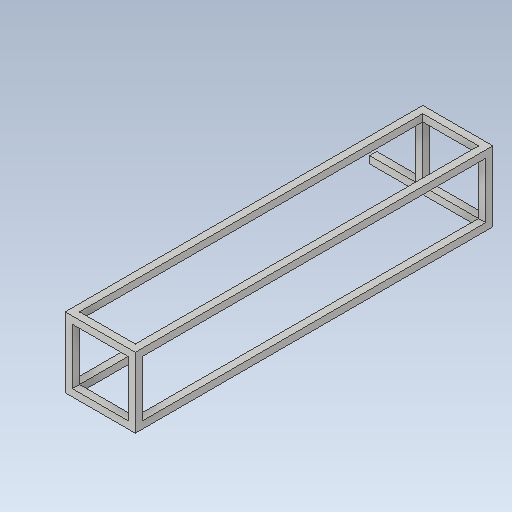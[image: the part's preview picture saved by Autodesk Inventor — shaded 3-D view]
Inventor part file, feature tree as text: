
AUTODESK INVENTOR PART (.ipt)
format: ipt  version: 2020 (Build 240168000, 168)  size: 321,024 bytes
history: native  units: mm
features: extrude x23, sketch x23
ambient origin geometry x8: Origin, YZ Plane, XZ Plane, XY Plane, X Axis, Y Axis, Z Axis, Center Point
bodies: Solid1 (feature_tree)
feature tree (46):
  extrude  "Extrusion1"  Depth=68.0mm
  extrude  "Extrusion2"  Depth=10.0mm
  extrude  "Extrusion3"  Depth=10.0mm
  extrude  "Extrusion4"  Depth=10.0mm TaperAngle=0.0deg
  extrude  "Extrusion5"  Depth=10.0mm
  extrude  "Extrusion6"  Depth=10.0mm
  extrude  "Extrusion7"  Depth=900.0mm TaperAngle=0.0deg
  extrude  "Extrusion8"  Depth=10.0mm TaperAngle=0.0deg
  extrude  "Extrusion9"  Depth=10.0mm TaperAngle=0.0deg
  extrude  "Extrusion10"  Depth=900.0mm TaperAngle=0.0deg
  extrude  "Extrusion11"  Depth=20.0mm
  extrude  "Extrusion12"  Depth=20.0mm
  extrude  "Extrusion13"  Depth=10.0mm TaperAngle=0.0deg
  extrude  "Extrusion14"  Depth=900.0mm TaperAngle=0.0deg
  extrude  "Extrusion15"  Depth=20.0mm
  extrude  "Extrusion16"  Depth=900.0mm TaperAngle=0.0deg
  extrude  "Extrusion17"  Depth=10.0mm TaperAngle=0.0deg
  extrude  "Extrusion18"  Depth=64.455mm TaperAngle=0.0deg
  extrude  "Extrusion19"  [1 undecoded]
  extrude  "Extrusion20"  [1 undecoded]
  extrude  "Extrusion21"  [1 undecoded]
  extrude  "Extrusion22"  [1 undecoded]
  extrude  "Extrusion24"  [1 undecoded]
  sketch  "Sketch1"  dims[d1=68.0mm d2=68.0mm]
  sketch  "Sketch2"  dims[d3=480.0mm d4=0.0mm d5=10.0mm]
  sketch  "Sketch3"  dims[d6=10.0mm d7=10.0mm]
  sketch  "Sketch4"  dims[d8=10.0mm d9=900.0mm d10=0.0mm]
  sketch  "Sketch5"  dims[d11=10.0mm d12=10.0mm]
  sketch  "Sketch6"  dims[d13=10.0mm d14=10.0mm]
  sketch  "Sketch7"  dims[d15=900.0mm d16=0.0mm d17=900.0mm d18=0.0mm]
  sketch  "Sketch8"  dims[d19=10.0mm d20=0.0mm d21=900.0mm d22=0.0mm]
  sketch  "Sketch9"  dims[d23=900.0mm d24=0.0mm d25=10.0mm d26=0.0mm]
  sketch  "Sketch10"  dims[d27=900.0mm d28=0.0mm d29=900.0mm d30=0.0mm]
  sketch  "Sketch11"  dims[d31=20.0mm d32=0.0mm d33=20.0mm]
  sketch  "Sketch12"  dims[d34=900.0mm d35=0.0mm d36=20.0mm]
  sketch  "Sketch13"  dims[d37=900.0mm d38=0.0mm d39=10.0mm d40=0.0mm]
  sketch  "Sketch14"  dims[d41=900.0mm d42=0.0mm d43=900.0mm d44=0.0mm]
  sketch  "Sketch15"  dims[d45=20.0mm d46=0.0mm d47=20.0mm]
  sketch  "Sketch16"  dims[d48=900.0mm d49=0.0mm d50=900.0mm d51=0.0mm]
  sketch  "Sketch17"  dims[d52=10.0mm d53=0.0mm d54=900.0mm d55=0.0mm]
  sketch  "Sketch18"  dims[d56=900.0mm d57=0.0mm d60=64.455mm d61=0.0mm]
  sketch  "Sketch19"
  sketch  "Sketch20"
  sketch  "Sketch21"
  sketch  "Sketch22"
  sketch  "Sketch24"
note: 5 required parameter values undecoded (feature->parameter linkage not recoverable at this tier; creation-order binding heuristic only, values carry confidence <= 0.55)
